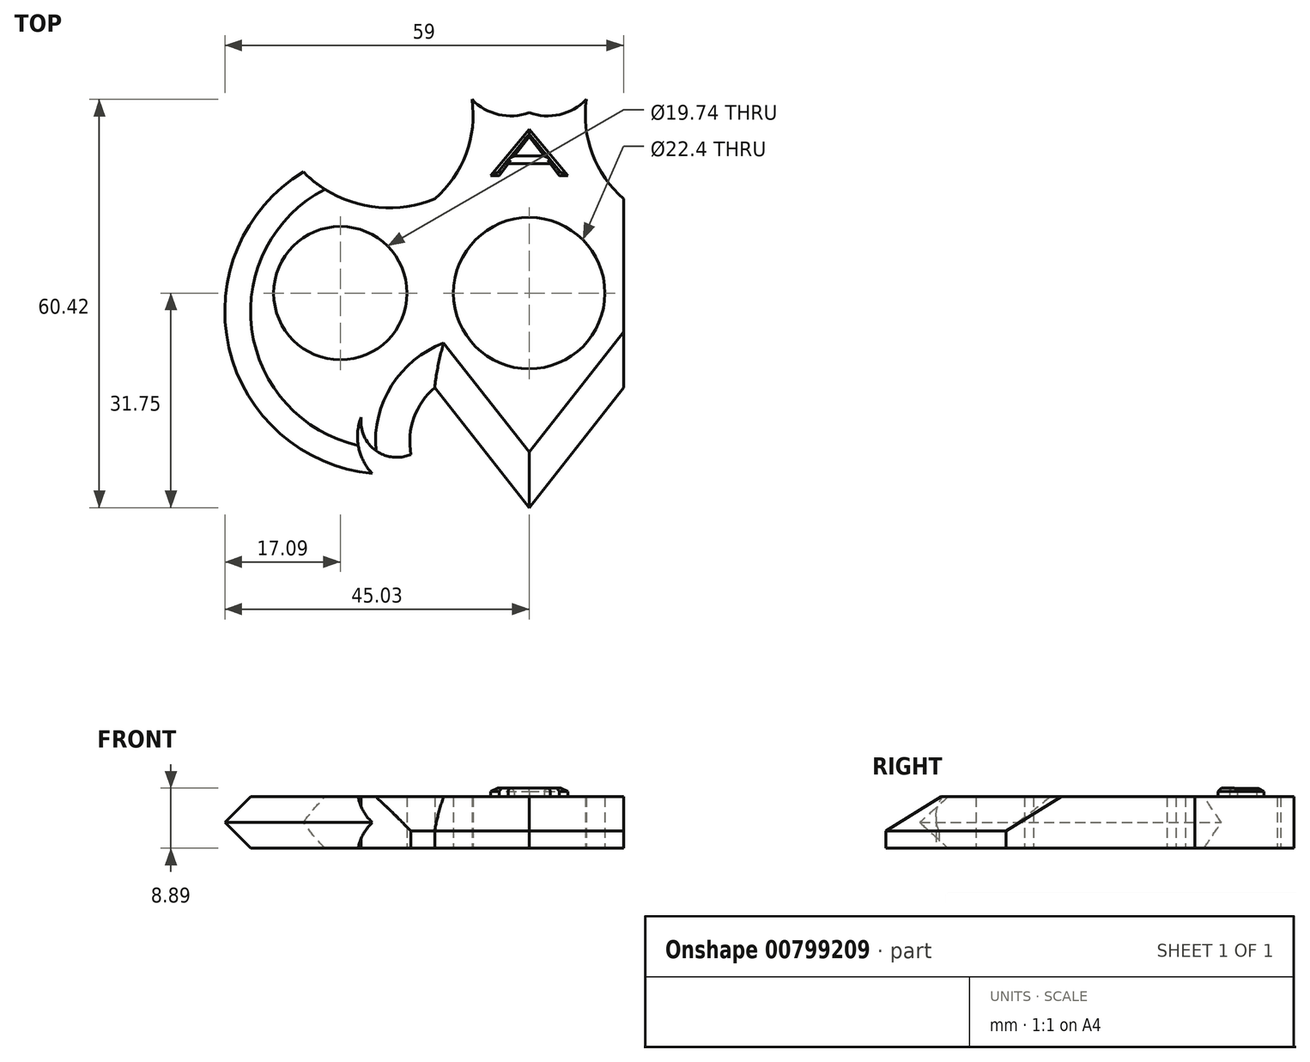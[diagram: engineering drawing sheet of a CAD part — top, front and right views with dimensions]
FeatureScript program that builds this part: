
annotation { "Feature Type Name" : "Feature", "Feature Type Description" : "" }
export const myFeature = defineFeature(function(context is Context, id is Id, definition is map)
    precondition{}
    {
        {
            var Q0;
            Q0=qCreatedBy(makeId("Top.planeOp"),FACE);
            var sketch = newSketch(context, id + "F0", { "sketchPlane" : qUnion([Q0])});
            skCircle(sketch, "E0", {"center": v(0, 0) * mm, "radius": 11.2 * mm});
            skLineSegment(sketch, "E1.bottom", {"start": v(13.97, -13.97) * mm, "end": v(-13.97, -13.97) * mm});
            skLineSegment(sketch, "E1.top", {"start": v(13.97, 13.97) * mm, "end": v(-13.97, 13.97) * mm});
            skLineSegment(sketch, "E1.left", {"start": v(13.97, -13.97) * mm, "end": v(13.97, 13.97) * mm});
            skLineSegment(sketch, "E1.right", {"start": v(-13.97, -13.97) * mm, "end": v(-13.97, 13.97) * mm});
            skArc(sketch, "E2", {"start": v(-34.3, 18.9) * mm, "mid": v(-24.93, 13.13) * mm, "end": v(-13.97, 13.97) * mm});
            skArc(sketch, "E3", {"start": v(-34.3, 18.9) * mm, "mid": v(-45.4, -9.38) * mm, "end": v(-21.46, -28.08) * mm});
            skLineSegment(sketch, "E4", {"start": v(-13.97, -13.97) * mm, "end": v(0, -31.75) * mm});
            skArc(sketch, "E5", {"start": v(-13.97, 13.97) * mm, "mid": v(-9.35, 20.62) * mm, "end": v(-8.45, 28.67) * mm});
            skArc(sketch, "E6", {"start": v(-8.45, 28.67) * mm, "mid": v(-4.52, 26.42) * mm, "end": v(0, 26.71) * mm});
            skLineSegment(sketch, "E7.MirrorCS", {"start": v(13.97, -13.97) * mm, "end": v(0, -31.75) * mm});
            skArc(sketch, "E8.MirrorCS", {"start": v(34.3, 18.9) * mm, "mid": v(24.93, 13.13) * mm, "end": v(13.97, 13.97) * mm});
            skArc(sketch, "E9.MirrorCS", {"start": v(34.3, 18.9) * mm, "mid": v(45.4, -9.38) * mm, "end": v(21.46, -28.08) * mm});
            skArc(sketch, "E10.MirrorCS", {"start": v(8.45, 28.67) * mm, "mid": v(4.52, 26.42) * mm, "end": v(0, 26.71) * mm});
            skArc(sketch, "E11.MirrorCS", {"start": v(13.97, 13.97) * mm, "mid": v(9.35, 20.62) * mm, "end": v(8.45, 28.67) * mm});
            skArc(sketch, "E12", {"start": v(-24.87, -18.38) * mm, "mid": v(-24.96, -23.86) * mm, "end": v(-21.46, -28.08) * mm});
            skArc(sketch, "E13", {"start": v(-24.87, -18.38) * mm, "mid": v(-22.77, -23.25) * mm, "end": v(-17.5, -23.86) * mm});
            skPoint(sketch, "E13.endSnap0", {"position": v(-24.96, -23.86) * mm});
            skArc(sketch, "E14", {"start": v(-13.97, -13.97) * mm, "mid": v(-17.05, -18.44) * mm, "end": v(-17.5, -23.86) * mm});
            skArc(sketch, "E15.MirrorCS", {"start": v(13.97, -13.97) * mm, "mid": v(17.05, -18.44) * mm, "end": v(17.5, -23.86) * mm});
            skPoint(sketch, "E16.MirrorP", {"position": v(24.96, -23.86) * mm});
            skArc(sketch, "E17.MirrorCS", {"start": v(24.87, -18.38) * mm, "mid": v(22.77, -23.25) * mm, "end": v(17.5, -23.86) * mm});
            skArc(sketch, "E18.MirrorCS", {"start": v(24.87, -18.38) * mm, "mid": v(24.96, -23.86) * mm, "end": v(21.46, -28.08) * mm});
            skCircle(sketch, "E19", {"center": v(-27.94, 0) * mm, "radius": 9.87 * mm});
            skCircle(sketch, "E20", {"center": v(27.94, 0) * mm, "radius": 9.87 * mm});
            skSolve(sketch);
        }
        {
            var Q0;
            Q0=makeQuery(id+"F0.imprint","IMPRINT",FACE,{"disambiguationData":[TD([[makeQuery(id+"F0.imprint","IMPRINT",EDGE,{"derivedFrom":sQuery(id+"F0.wireOp",EDGE,"E1.right")}),1.0]])]});
            var Q1;
            Q1=makeQuery(id+"F0.imprint","IMPRINT",FACE,{"disambiguationData":[TD([[makeQuery(id+"F0.imprint","IMPRINT",EDGE,{"derivedFrom":sQuery(id+"F0.wireOp",EDGE,"E1.top")}),-1.0]])]});
            var Q2;
            Q2=makeQuery(id+"F0.imprint","IMPRINT",FACE,{"disambiguationData":[TD([[makeQuery(id+"F0.imprint","IMPRINT",EDGE,{"derivedFrom":sQuery(id+"F0.wireOp",EDGE,"E0")}),-1.0]])]});
            var Q3;
            Q3=makeQuery(id+"F0.imprint","IMPRINT",FACE,{"disambiguationData":[TD([[makeQuery(id+"F0.imprint","IMPRINT",EDGE,{"derivedFrom":sQuery(id+"F0.wireOp",EDGE,"E8.MirrorCS")}),1.0]])]});
            var Q4;
            Q4=makeQuery(id+"F0.imprint","IMPRINT",FACE,{"disambiguationData":[TD([[makeQuery(id+"F0.imprint","IMPRINT",EDGE,{"derivedFrom":sQuery(id+"F0.wireOp",EDGE,"E1.bottom")}),1.0]])]});
            extrude(context, id + "F1", {"entities" : qUnion([Q0, Q1, Q2, Q3, Q4]), "depth" : 7.62 * mm, "offsetDistance" : 25.4 * mm});
        }
        {
            var Q0;
            Q0=makeQuery(id+"F1.opExtrude","CAP_EDGE",EDGE,{"disambiguationData":[OSD([sQuery(id+"F0.wireOp",EDGE,"E4")])],"isStart":false});
            var Q1;
            Q1=makeQuery(id+"F1.opExtrude","CAP_EDGE",EDGE,{"disambiguationData":[OSD([sQuery(id+"F0.wireOp",EDGE,"E7.MirrorCS")])],"isStart":false});
            var Q2;
            Q2=makeQuery(id+"F1.opExtrude","CAP_EDGE",EDGE,{"disambiguationData":[OSD([sQuery(id+"F0.wireOp",EDGE,"E14")])],"isStart":false});
            var Q3;
            Q3=makeQuery(id+"F1.opExtrude","CAP_EDGE",EDGE,{"disambiguationData":[OSD([sQuery(id+"F0.wireOp",EDGE,"E15.MirrorCS")])],"isStart":false});
            var Q4;
            Q4=makeQuery(id+"F1.opExtrude","CAP_EDGE",EDGE,{"disambiguationData":[OSD([sQuery(id+"F0.wireOp",EDGE,"E9.MirrorCS")])],"isStart":false});
            var Q5;
            Q5=makeQuery(id+"F1.opExtrude","CAP_EDGE",EDGE,{"disambiguationData":[OSD([sQuery(id+"F0.wireOp",EDGE,"E3")])],"isStart":false});
            var Q6;
            Q6=makeQuery(id+"F1.opExtrude","CAP_EDGE",EDGE,{"disambiguationData":[OSD([sQuery(id+"F0.wireOp",EDGE,"E3")])],"isStart":true});
            var Q7;
            Q7=makeQuery(id+"F1.opExtrude","CAP_EDGE",EDGE,{"disambiguationData":[OSD([sQuery(id+"F0.wireOp",EDGE,"E9.MirrorCS")])],"isStart":true});
            chamfer(context, id + "F2", {"entities" : qUnion([Q0, Q1, Q2, Q3, Q4, Q5, Q6, Q7]), "width" : 5.08 * mm, "tangentPropagation" : true});
        }
        {
            var Q0;
            Q0=makeQuery(id+"F1.opExtrude","CAP_FACE",FACE,{"disambiguationData":[OSD([sQuery(id+"F0.wireOp",EDGE,"E0"),sQuery(id+"F0.wireOp",EDGE,"E2"),sQuery(id+"F0.wireOp",EDGE,"E3"),sQuery(id+"F0.wireOp",EDGE,"E4"),sQuery(id+"F0.wireOp",EDGE,"E5"),sQuery(id+"F0.wireOp",EDGE,"E6"),sQuery(id+"F0.wireOp",EDGE,"E7.MirrorCS"),sQuery(id+"F0.wireOp",EDGE,"E8.MirrorCS"),sQuery(id+"F0.wireOp",EDGE,"E9.MirrorCS"),sQuery(id+"F0.wireOp",EDGE,"E10.MirrorCS"),sQuery(id+"F0.wireOp",EDGE,"E11.MirrorCS"),sQuery(id+"F0.wireOp",EDGE,"E12"),sQuery(id+"F0.wireOp",EDGE,"E13"),sQuery(id+"F0.wireOp",EDGE,"E14"),sQuery(id+"F0.wireOp",EDGE,"E15.MirrorCS"),sQuery(id+"F0.wireOp",EDGE,"E17.MirrorCS"),sQuery(id+"F0.wireOp",EDGE,"E18.MirrorCS"),sQuery(id+"F0.wireOp",EDGE,"E19"),sQuery(id+"F0.wireOp",EDGE,"E20")])],"isStart":false});
            var sketch = newSketch(context, id + "F3", { "sketchPlane" : qUnion([Q0])});
            skLineSegment(sketch, "E21", {"start": v(0, 24.22) * mm, "end": v(-5.72, 17.42) * mm});
            skLineSegment(sketch, "E22", {"start": v(-5.72, 17.42) * mm, "end": v(-4.45, 17.42) * mm});
            skLineSegment(sketch, "E23", {"start": v(-4.45, 17.42) * mm, "end": v(0, 23.15) * mm});
            skLineSegment(sketch, "E24.MirrorCS", {"start": v(4.45, 17.42) * mm, "end": v(0, 23.15) * mm});
            skLineSegment(sketch, "E25.MirrorCS", {"start": v(5.72, 17.42) * mm, "end": v(4.45, 17.42) * mm});
            skLineSegment(sketch, "E26.MirrorCS", {"start": v(0, 24.22) * mm, "end": v(5.72, 17.42) * mm});
            skLineSegment(sketch, "E27", {"start": v(-2.22, 20.28) * mm, "end": v(2.22, 20.28) * mm});
            skLineSegment(sketch, "E28", {"start": v(-3.11, 19.14) * mm, "end": v(3.11, 19.14) * mm});
            skSolve(sketch);
        }
        {
            var Q0;
            Q0=makeQuery(id+"F3.imprint","IMPRINT",FACE,{"disambiguationData":[TD([[makeQuery(id+"F3.imprint","IMPRINT",EDGE,{"derivedFrom":sQuery(id+"F3.wireOp",EDGE,"E21")}),1.0]])]});
            var Q1;
            {var subQ0=sQuery(id+"F3.wireOp",EDGE,"E27");Q1=makeQuery(id+"F3.imprint","IMPRINT",FACE,{"disambiguationData":[TD([[makeQuery(id+"F3.imprint","IMPRINT",EDGE,{"derivedFrom":subQ0}),-1.0]])]});}
            extrude(context, id + "F4", {"entities" : qUnion([Q0, Q1]), "operationType" : NewBodyOperationType.ADD, "depth" : 1.27 * mm, "offsetDistance" : 25.4 * mm});
        }
        {
            var Q0;
            Q0=makeQuery(id+"F4.opExtrude","CAP_EDGE",EDGE,{"disambiguationData":[OSD([sQuery(id+"F3.wireOp",EDGE,"E28")])],"isStart":false});
            var Q1;
            Q1=makeQuery(id+"F4.opExtrude","CAP_EDGE",EDGE,{"disambiguationData":[OSD([sQuery(id+"F3.wireOp",EDGE,"E27")])],"isStart":false});
            var Q2;
            {var subQ0=sQuery(id+"F3.wireOp",EDGE,"E23");Q2=makeQuery(id+"F4.opExtrude","CAP_EDGE",EDGE,{"disambiguationData":[OSD([subQ0]),TDD([makeQuery(id+"F3.imprint","IMPRINT",EDGE,{"disambiguationData":[TD([[makeQuery(id+"F3.imprint","INTERSECT",VERTEX,{"derivedFrom":[subQ0,sQuery(id+"F3.wireOp",EDGE,"E24.MirrorCS")]}),1.0]])],"derivedFrom":subQ0})])],"isStart":false});}
            var Q3;
            {var subQ0=sQuery(id+"F3.wireOp",EDGE,"E24.MirrorCS");Q3=makeQuery(id+"F4.opExtrude","CAP_EDGE",EDGE,{"disambiguationData":[OSD([subQ0]),TDD([makeQuery(id+"F3.imprint","IMPRINT",EDGE,{"disambiguationData":[TD([[makeQuery(id+"F3.imprint","INTERSECT",VERTEX,{"derivedFrom":[sQuery(id+"F3.wireOp",EDGE,"E23"),subQ0]}),1.0]])],"derivedFrom":subQ0})])],"isStart":false});}
            fillet(context, id + "F5", {"entities" : qUnion([Q0, Q1, Q2, Q3]), "radius" : 0.5 * mm, "tangentPropagation" : true, "allowEdgeOverflow" : false});
        }
        {
            var Q0;
            Q0=makeQuery(id+"F4.opExtrude","CAP_EDGE",EDGE,{"disambiguationData":[OSD([sQuery(id+"F3.wireOp",EDGE,"E22")])],"isStart":false});
            var Q1;
            Q1=makeQuery(id+"F4.opExtrude","CAP_EDGE",EDGE,{"disambiguationData":[OSD([sQuery(id+"F3.wireOp",EDGE,"E25.MirrorCS")])],"isStart":false});
            var Q2;
            Q2=makeQuery(id+"F4.opExtrude","CAP_EDGE",EDGE,{"disambiguationData":[OSD([sQuery(id+"F3.wireOp",EDGE,"E21")])],"isStart":false});
            chamfer(context, id + "F6", {"entities" : qUnion([Q0, Q1, Q2]), "width" : 0.5 * mm, "tangentPropagation" : true});
        }
        {
            var Q0;
            Q0=makeQuery(id+"F4.opExtrude","CAP_EDGE",EDGE,{"disambiguationData":[OSD([sQuery(id+"F3.wireOp",EDGE,"E26.MirrorCS")])],"isStart":false});
            chamfer(context, id + "F7", {"entities" : qUnion([Q0]), "width" : 0.5 * mm, "tangentPropagation" : true});
        }
    });
